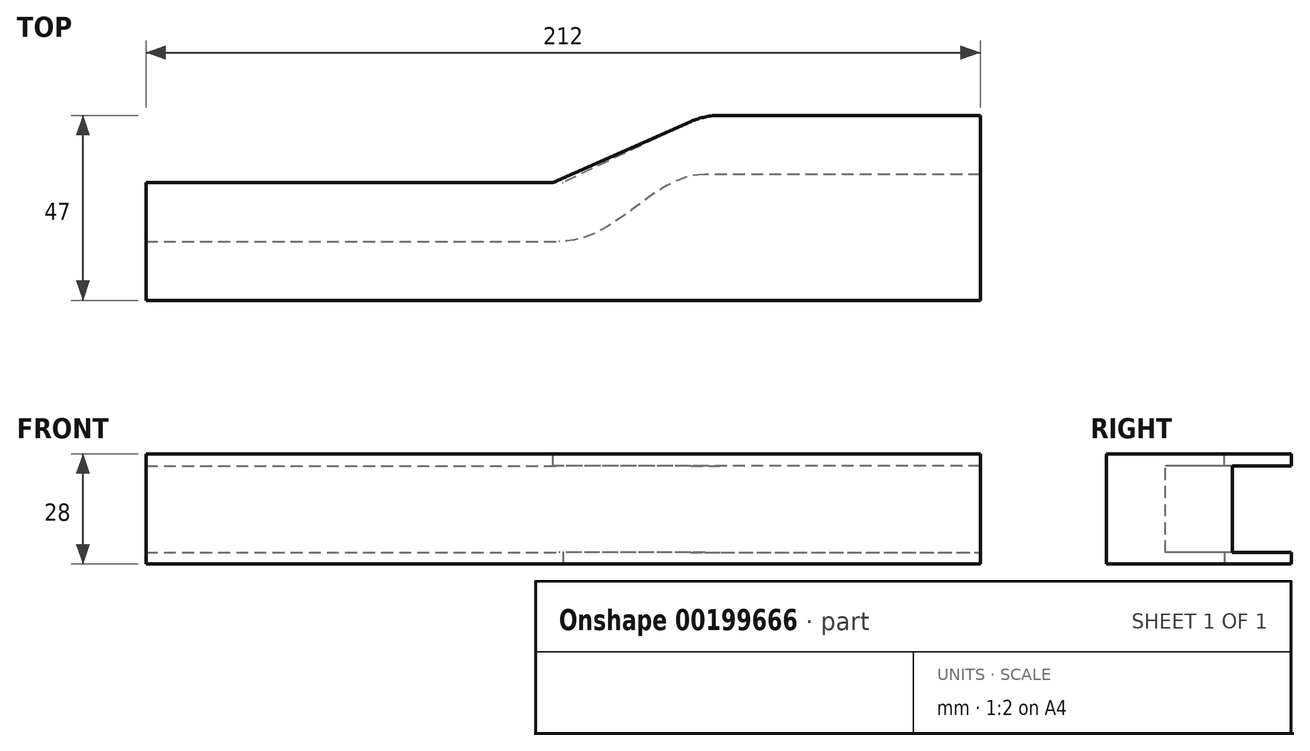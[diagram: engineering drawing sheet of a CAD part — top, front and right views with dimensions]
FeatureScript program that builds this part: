
annotation { "Feature Type Name" : "Feature", "Feature Type Description" : "" }
export const myFeature = defineFeature(function(context is Context, id is Id, definition is map)
    precondition{}
    {
        {
            var Q0;
            Q0=qCreatedBy(makeId("Top.planeOp"),FACE);
            var sketch = newSketch(context, id + "F0", { "sketchPlane" : qUnion([Q0])});
            skLineSegment(sketch, "E0", {"start": v(-81.7, 0) * mm, "end": v(23.3, 0) * mm});
            skLineSegment(sketch, "E1", {"start": v(23.3, 0) * mm, "end": v(23.3, 17) * mm, "construction": true});
            skLineSegment(sketch, "E2", {"start": v(23.3, 17) * mm, "end": v(60.3, 17) * mm, "construction": true});
            skLineSegment(sketch, "E3", {"start": v(60.3, 17) * mm, "end": v(130.3, 17) * mm});
            skLineSegment(sketch, "E4", {"start": v(130.3, 17) * mm, "end": v(130.3, -15) * mm});
            skLineSegment(sketch, "E5", {"start": v(130.3, -15) * mm, "end": v(-81.7, -15) * mm});
            skLineSegment(sketch, "E6", {"start": v(-81.7, -15) * mm, "end": v(-81.7, 0) * mm});
            skFitSpline(sketch, "E7", {"points": [v(60.3, 17) * mm, v(23.3, 0) * mm], "startDerivative": vector(-39.76, 0) * mm, "endDerivative": vector(-44.92, 0) * mm});
            skSolve(sketch);
        }
        {
            var Q0;
            Q0=makeQuery(id+"F0.imprint","IMPRINT",FACE,{"disambiguationData":[TD([[makeQuery(id+"F0.imprint","IMPRINT",EDGE,{"derivedFrom":sQuery(id+"F0.wireOp",EDGE,"E0")}),-1.0]])]});
            var Q1;
            Q1 = qSketchRegion(id + "F0", true);
            extrude(context, id + "F1", {"entities" : qUnion([Q0, Q1]), "oppositeDirection" : true, "depth" : 28 * mm});
        }
        {
            var Q0;
            Q0=makeQuery(id+"F1.opExtrude","SWEPT_FACE",FACE,{"disambiguationData":[OSD([sQuery(id+"F0.wireOp",EDGE,"E0")])]});
            var sketch = newSketch(context, id + "F2", { "sketchPlane" : qUnion([Q0])});
            skLineSegment(sketch, "E8.bottom", {"start": v(81.7, 0) * mm, "end": v(-130.2, 0) * mm});
            skLineSegment(sketch, "E8.top", {"start": v(81.7, -3) * mm, "end": v(-130.2, -3) * mm});
            skLineSegment(sketch, "E8.left", {"start": v(81.7, 0) * mm, "end": v(81.7, -3) * mm});
            skLineSegment(sketch, "E8.right", {"start": v(-130.2, 0) * mm, "end": v(-130.2, -3) * mm});
            skLineSegment(sketch, "E9.bottom", {"start": v(81.7, -28) * mm, "end": v(-130.2, -28) * mm});
            skLineSegment(sketch, "E9.top", {"start": v(81.7, -25) * mm, "end": v(-130.2, -25) * mm});
            skLineSegment(sketch, "E9.left", {"start": v(81.7, -28) * mm, "end": v(81.7, -25) * mm});
            skLineSegment(sketch, "E9.right", {"start": v(-130.2, -28) * mm, "end": v(-130.2, -25) * mm});
            skSolve(sketch);
        }
        {
            var Q0;
            Q0 = qSketchRegion(id + "F2", true);
            extrude(context, id + "F3", {"entities" : qUnion([Q0]), "operationType" : NewBodyOperationType.ADD, "depth" : 15 * mm});
        }
        {
            var Q0;
            Q0=makeQuery(id+"F1.opExtrude","SWEPT_FACE",FACE,{"disambiguationData":[OSD([sQuery(id+"F0.wireOp",EDGE,"E3")])]});
            var sketch = newSketch(context, id + "F4", { "sketchPlane" : qUnion([Q0])});
            skLineSegment(sketch, "E10.bottom", {"start": v(-60.3, -28) * mm, "end": v(-130.3, -28) * mm});
            skLineSegment(sketch, "E10.top", {"start": v(-60.3, -25) * mm, "end": v(-130.3, -25) * mm});
            skLineSegment(sketch, "E10.left", {"start": v(-60.3, -28) * mm, "end": v(-60.3, -25) * mm});
            skLineSegment(sketch, "E10.right", {"start": v(-130.3, -28) * mm, "end": v(-130.3, -25) * mm});
            skLineSegment(sketch, "E11.bottom", {"start": v(-130.3, 0) * mm, "end": v(-60.3, 0) * mm});
            skLineSegment(sketch, "E11.top", {"start": v(-130.3, -3) * mm, "end": v(-60.3, -3) * mm});
            skLineSegment(sketch, "E11.left", {"start": v(-130.3, 0) * mm, "end": v(-130.3, -3) * mm});
            skLineSegment(sketch, "E11.right", {"start": v(-60.3, 0) * mm, "end": v(-60.3, -3) * mm});
            skSolve(sketch);
        }
        {
            var Q0;
            Q0 = qSketchRegion(id + "F4", true);
            extrude(context, id + "F5", {"entities" : qUnion([Q0]), "operationType" : NewBodyOperationType.ADD, "depth" : 15 * mm});
        }
        {
            var Q0;
            Q0=makeQuery(id+"F5.boolean.opBoolean","MERGE",FACE,{"derivedFrom":[makeQuery(id+"F3.boolean.opBoolean","MERGE",FACE,{"derivedFrom":[makeQuery(id+"F1.opExtrude","CAP_FACE",FACE,{"disambiguationData":[OSD([sQuery(id+"F0.wireOp",EDGE,"E0"),sQuery(id+"F0.wireOp",EDGE,"E3"),sQuery(id+"F0.wireOp",EDGE,"E4"),sQuery(id+"F0.wireOp",EDGE,"E5"),sQuery(id+"F0.wireOp",EDGE,"E6"),sQuery(id+"F0.wireOp",EDGE,"E7")])],"isStart":true}),makeQuery(id+"F3.opExtrude","SWEPT_FACE",FACE,{"disambiguationData":[OSD([sQuery(id+"F2.wireOp",EDGE,"E8.bottom")])]})]}),makeQuery(id+"F5.opExtrude","SWEPT_FACE",FACE,{"disambiguationData":[OSD([sQuery(id+"F4.wireOp",EDGE,"E11.bottom")])]})]});
            var sketch = newSketch(context, id + "F6", { "sketchPlane" : qUnion([Q0])});
            skLineSegment(sketch, "E12", {"start": v(60.3, 32) * mm, "end": v(21.74, 15) * mm});
            skLineSegment(sketch, "E13", {"start": v(21.74, 15) * mm, "end": v(26.04, -15) * mm});
            skLineSegment(sketch, "E14", {"start": v(26.04, -15) * mm, "end": v(64.8, 0) * mm});
            skLineSegment(sketch, "E15", {"start": v(64.8, 0) * mm, "end": v(60.3, 32) * mm});
            skSolve(sketch);
        }
        {
            var Q0;
            Q0 = qSketchRegion(id + "F6", true);
            extrude(context, id + "F7", {"entities" : qUnion([Q0]), "operationType" : NewBodyOperationType.ADD, "oppositeDirection" : true, "depth" : 3 * mm});
        }
        {
            var Q0;
            {var subQ0=sQuery(id+"F4.wireOp",EDGE,"E11.right");Q0=makeQuery(id+"F7.boolean.opBoolean","MERGE",EDGE,{"derivedFrom":[makeQuery(id+"F5.opExtrude","CAP_EDGE",EDGE,{"disambiguationData":[OSD([subQ0])],"isStart":false}),makeQuery(id+"F7.opExtrude","SWEPT_EDGE",EDGE,{"disambiguationData":[OSD([sQuery(id+"F4.wireOp",EDGE,"E11.bottom"),subQ0,sQuery(id+"F6.wireOp",EDGE,"E12"),sQuery(id+"F6.wireOp",EDGE,"E15")])]})]});}
            var Q1;
            Q1=makeQuery(id+"F7.opExtrude","SWEPT_EDGE",EDGE,{"disambiguationData":[OSD([sQuery(id+"F2.wireOp",EDGE,"E8.bottom"),sQuery(id+"F6.wireOp",EDGE,"E12"),sQuery(id+"F6.wireOp",EDGE,"E13")])]});
            fillet(context, id + "F8", {"entities" : qUnion([Q0, Q1]), "radius" : 18.22 * mm, "tangentPropagation" : true, "allowEdgeOverflow" : false});
        }
        {
            var Q0;
            Q0=makeQuery(id+"F5.boolean.opBoolean","MERGE",FACE,{"derivedFrom":[makeQuery(id+"F3.boolean.opBoolean","MERGE",FACE,{"derivedFrom":[makeQuery(id+"F1.opExtrude","CAP_FACE",FACE,{"disambiguationData":[OSD([sQuery(id+"F0.wireOp",EDGE,"E0"),sQuery(id+"F0.wireOp",EDGE,"E3"),sQuery(id+"F0.wireOp",EDGE,"E4"),sQuery(id+"F0.wireOp",EDGE,"E5"),sQuery(id+"F0.wireOp",EDGE,"E6"),sQuery(id+"F0.wireOp",EDGE,"E7")])],"isStart":false}),makeQuery(id+"F3.opExtrude","SWEPT_FACE",FACE,{"disambiguationData":[OSD([sQuery(id+"F2.wireOp",EDGE,"E9.bottom")])]})]}),makeQuery(id+"F5.opExtrude","SWEPT_FACE",FACE,{"disambiguationData":[OSD([sQuery(id+"F4.wireOp",EDGE,"E10.bottom")])]})]});
            var sketch = newSketch(context, id + "F9", { "sketchPlane" : qUnion([Q0])});
            skLineSegment(sketch, "E16", {"start": v(60.3, -32) * mm, "end": v(24.3, -15) * mm});
            skPoint(sketch, "E16.endSnap0", {"position": v(24.3, 15) * mm});
            skPoint(sketch, "E17.orphan", {"position": v(60.3, 15) * mm});
            skLineSegment(sketch, "E18", {"start": v(60.3, -32) * mm, "end": v(60.3, -17) * mm});
            skLineSegment(sketch, "E19", {"start": v(60.3, -17) * mm, "end": v(52.3, -15) * mm});
            skLineSegment(sketch, "E20", {"start": v(52.3, -15) * mm, "end": v(24.3, -15) * mm});
            skSolve(sketch);
        }
        {
            var Q0;
            Q0 = qSketchRegion(id + "F9", true);
            extrude(context, id + "F10", {"entities" : qUnion([Q0]), "operationType" : NewBodyOperationType.ADD, "oppositeDirection" : true, "depth" : 3 * mm});
        }
        {
            var Q0;
            Q0=makeQuery(id+"F10.boolean.opBoolean","MERGE",EDGE,{"derivedFrom":[makeQuery(id+"F5.opExtrude","CAP_EDGE",EDGE,{"disambiguationData":[OSD([sQuery(id+"F4.wireOp",EDGE,"E10.left")])],"isStart":false}),makeQuery(id+"F10.opExtrude","SWEPT_EDGE",EDGE,{"disambiguationData":[OSD([sQuery(id+"F4.wireOp",EDGE,"E10.bottom"),sQuery(id+"F9.wireOp",EDGE,"E16"),sQuery(id+"F9.wireOp",EDGE,"E18")])]})]});
            var Q1;
            Q1=makeQuery(id+"F10.opExtrude","SWEPT_EDGE",EDGE,{"disambiguationData":[OSD([sQuery(id+"F2.wireOp",EDGE,"E9.bottom"),sQuery(id+"F9.wireOp",EDGE,"E16"),sQuery(id+"F9.wireOp",EDGE,"E20")])]});
            fillet(context, id + "F11", {"entities" : qUnion([Q0, Q1]), "radius" : 18.22 * mm, "tangentPropagation" : true, "allowEdgeOverflow" : false});
        }
    });
